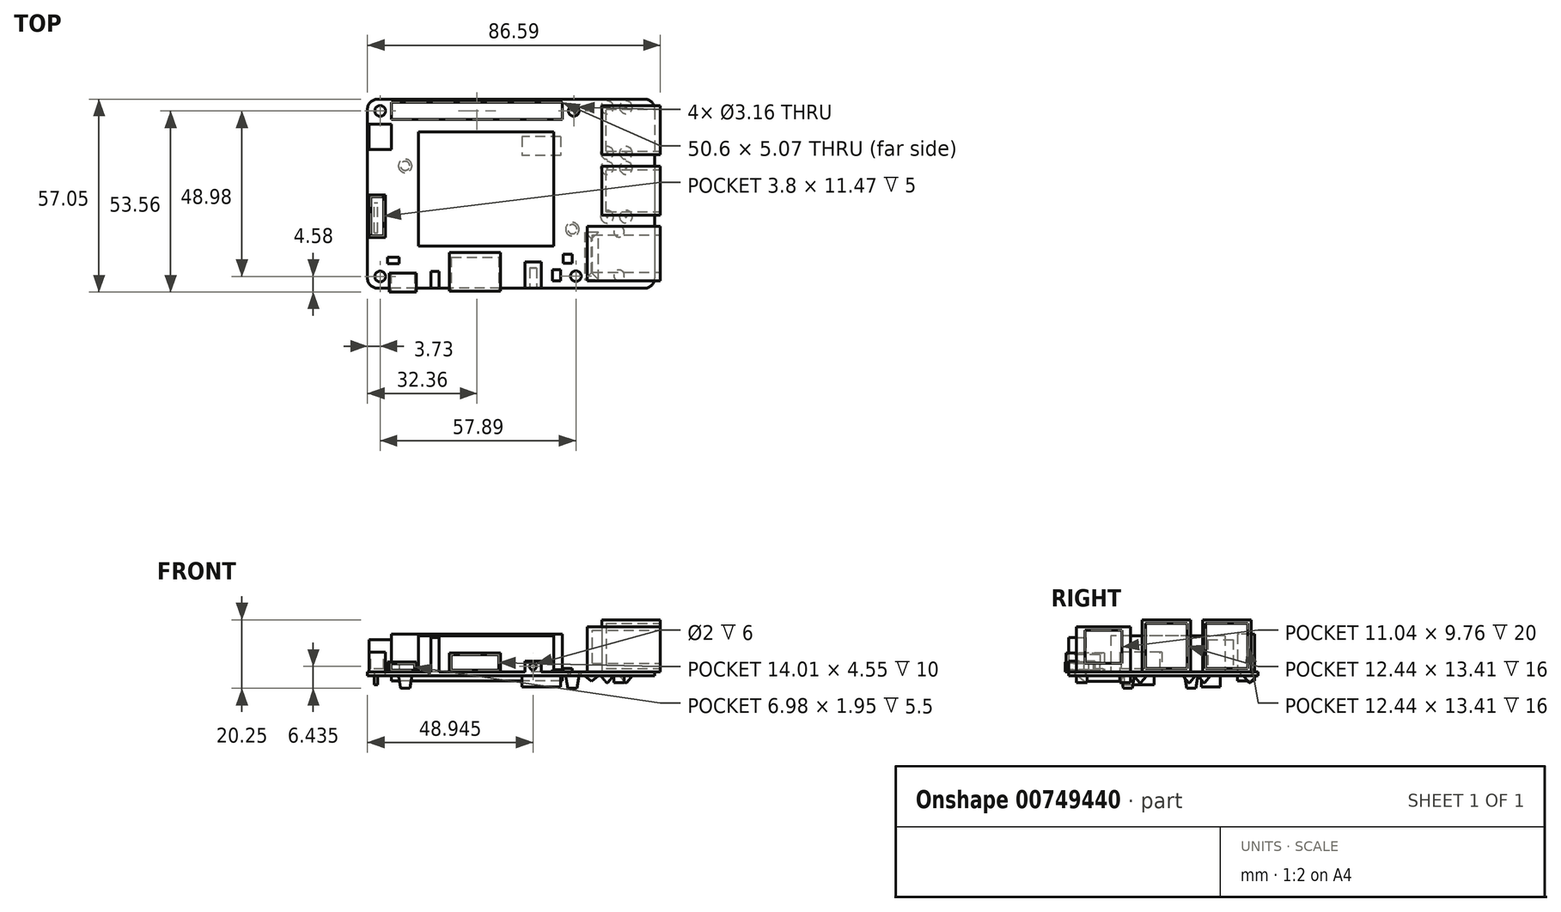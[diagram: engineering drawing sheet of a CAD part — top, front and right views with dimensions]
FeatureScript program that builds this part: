
annotation { "Feature Type Name" : "Feature", "Feature Type Description" : "" }
export const myFeature = defineFeature(function(context is Context, id is Id, definition is map)
    precondition{}
    {
        {
            var Q0;
            Q0=qCreatedBy(makeId("Top.planeOp"),FACE);
            var sketch = newSketch(context, id + "F0", { "sketchPlane" : qUnion([Q0])});
            skLineSegment(sketch, "E0.bottom", {"start": v(42.46, 27.98) * mm, "end": v(-42.46, 27.98) * mm});
            skLineSegment(sketch, "E0.top", {"start": v(42.46, -27.98) * mm, "end": v(-42.46, -27.98) * mm});
            skLineSegment(sketch, "E0.left", {"start": v(42.46, 27.98) * mm, "end": v(42.46, -27.98) * mm});
            skLineSegment(sketch, "E0.right", {"start": v(-42.46, 27.98) * mm, "end": v(-42.46, -27.98) * mm});
            skPoint(sketch, "E0.middle", {"position": v(0, 0) * mm});
            skSolve(sketch);
        }
        {
            var Q0;
            Q0 = qSketchRegion(id + "F0", true);
            extrude(context, id + "F1", {"entities" : qUnion([Q0]), "depth" : 1.15 * mm, "offsetDistance" : 25 * mm});
        }
        {
            var Q0;
            Q0=makeQuery(id+"F1.opExtrude","CAP_FACE",FACE,{"disambiguationData":[OSD([sQuery(id+"F0.wireOp",EDGE,"E0.bottom"),sQuery(id+"F0.wireOp",EDGE,"E0.top"),sQuery(id+"F0.wireOp",EDGE,"E0.left"),sQuery(id+"F0.wireOp",EDGE,"E0.right")])],"isStart":false});
            var sketch = newSketch(context, id + "F2", { "sketchPlane" : qUnion([Q0])});
            skLineSegment(sketch, "E1.top", {"start": v(44.05, -9.69) * mm, "end": v(22.48, -9.69) * mm});
            skLineSegment(sketch, "E1.left", {"start": v(44.05, -25.73) * mm, "end": v(44.05, -9.69) * mm});
            skLineSegment(sketch, "E1.right", {"start": v(22.48, -25.73) * mm, "end": v(22.48, -9.69) * mm});
            skLineSegment(sketch, "E2", {"start": v(44.05, -25.73) * mm, "end": v(22.48, -25.73) * mm});
            skSolve(sketch);
        }
        {
            var Q0;
            Q0 = qSketchRegion(id + "F2", true);
            extrude(context, id + "F3", {"entities" : qUnion([Q0]), "operationType" : NewBodyOperationType.ADD, "depth" : 13.33 * mm, "offsetDistance" : 25 * mm});
        }
        {
            var Q0;
            Q0=makeQuery(id+"F3.opExtrude","SWEPT_FACE",FACE,{"disambiguationData":[OSD([sQuery(id+"F2.wireOp",EDGE,"E1.left")])]});
            var sketch = newSketch(context, id + "F4", { "sketchPlane" : qUnion([Q0])});
            skLineSegment(sketch, "E3", {"start": v(-23.23, 13.45) * mm, "end": v(-12.19, 13.45) * mm});
            skLineSegment(sketch, "E4", {"start": v(-23.23, 3.7) * mm, "end": v(-23.23, 13.45) * mm});
            skLineSegment(sketch, "E5", {"start": v(-23.23, 3.7) * mm, "end": v(-12.19, 3.7) * mm});
            skLineSegment(sketch, "E6", {"start": v(-12.19, 3.7) * mm, "end": v(-12.19, 13.45) * mm});
            skSolve(sketch);
        }
        {
            var Q0;
            Q0 = qSketchRegion(id + "F4", true);
            extrude(context, id + "F5", {"entities" : qUnion([Q0]), "operationType" : NewBodyOperationType.REMOVE, "oppositeDirection" : true, "depth" : 20 * mm, "offsetDistance" : 25 * mm});
        }
        {
            var Q0;
            Q0=makeQuery(id+"F1.opExtrude","CAP_FACE",FACE,{"disambiguationData":[OSD([sQuery(id+"F0.wireOp",EDGE,"E0.bottom"),sQuery(id+"F0.wireOp",EDGE,"E0.top"),sQuery(id+"F0.wireOp",EDGE,"E0.left"),sQuery(id+"F0.wireOp",EDGE,"E0.right")])],"isStart":false});
            var sketch = newSketch(context, id + "F6", { "sketchPlane" : qUnion([Q0])});
            skLineSegment(sketch, "E7", {"start": v(42.46, -25.73) * mm, "end": v(42.46, 8.12) * mm});
            skLineSegment(sketch, "E8", {"start": v(42.46, 8.12) * mm, "end": v(44.13, 8.12) * mm});
            skLineSegment(sketch, "E9.bottom", {"start": v(44.13, 8.12) * mm, "end": v(26.87, 8.12) * mm});
            skLineSegment(sketch, "E9.top", {"start": v(44.13, -6.32) * mm, "end": v(26.87, -6.32) * mm});
            skLineSegment(sketch, "E9.left", {"start": v(44.13, 8.12) * mm, "end": v(44.13, -6.32) * mm});
            skLineSegment(sketch, "E9.right", {"start": v(26.87, 8.12) * mm, "end": v(26.87, -6.32) * mm});
            skLineSegment(sketch, "E10", {"start": v(42.46, -25.73) * mm, "end": v(42.46, 26.01) * mm});
            skLineSegment(sketch, "E11", {"start": v(42.46, 26.01) * mm, "end": v(44.13, 26.01) * mm});
            skLineSegment(sketch, "E12.bottom", {"start": v(44.13, 26.01) * mm, "end": v(26.87, 26.01) * mm});
            skLineSegment(sketch, "E12.top", {"start": v(44.13, 11.57) * mm, "end": v(26.87, 11.57) * mm});
            skLineSegment(sketch, "E12.left", {"start": v(44.13, 26.01) * mm, "end": v(44.13, 11.57) * mm});
            skLineSegment(sketch, "E12.right", {"start": v(26.87, 26.01) * mm, "end": v(26.87, 11.57) * mm});
            skSolve(sketch);
        }
        {
            var Q0;
            Q0 = qSketchRegion(id + "F6", true);
            extrude(context, id + "F7", {"entities" : qUnion([Q0]), "operationType" : NewBodyOperationType.ADD, "depth" : 15.4 * mm, "offsetDistance" : 25 * mm});
        }
        {
            var Q0;
            Q0=makeQuery(id+"F7.opExtrude","SWEPT_FACE",FACE,{"disambiguationData":[OSD([sQuery(id+"F6.wireOp",EDGE,"E9.left")])]});
            var sketch = newSketch(context, id + "F8", { "sketchPlane" : qUnion([Q0])});
            skLineSegment(sketch, "E13.bottom", {"start": v(-5.32, 15.56) * mm, "end": v(7.12, 15.56) * mm});
            skLineSegment(sketch, "E13.top", {"start": v(-5.32, 2.15) * mm, "end": v(7.12, 2.15) * mm});
            skLineSegment(sketch, "E13.left", {"start": v(-5.32, 15.56) * mm, "end": v(-5.32, 2.15) * mm});
            skLineSegment(sketch, "E13.right", {"start": v(7.12, 15.56) * mm, "end": v(7.12, 2.15) * mm});
            skSolve(sketch);
        }
        {
            var Q0;
            Q0 = qSketchRegion(id + "F8", true);
            extrude(context, id + "F9", {"entities" : qUnion([Q0]), "operationType" : NewBodyOperationType.REMOVE, "oppositeDirection" : true, "depth" : 16 * mm, "offsetDistance" : 25 * mm});
        }
        {
            var Q0;
            Q0=makeQuery(id+"F7.opExtrude","SWEPT_FACE",FACE,{"disambiguationData":[OSD([sQuery(id+"F6.wireOp",EDGE,"E12.left")])]});
            var sketch = newSketch(context, id + "F10", { "sketchPlane" : qUnion([Q0])});
            skLineSegment(sketch, "E14.bottom", {"start": v(12.57, 15.56) * mm, "end": v(25.01, 15.56) * mm});
            skLineSegment(sketch, "E14.top", {"start": v(12.57, 2.15) * mm, "end": v(25.01, 2.15) * mm});
            skLineSegment(sketch, "E14.left", {"start": v(12.57, 15.56) * mm, "end": v(12.57, 2.15) * mm});
            skLineSegment(sketch, "E14.right", {"start": v(25.01, 15.56) * mm, "end": v(25.01, 2.15) * mm});
            skSolve(sketch);
        }
        {
            var Q0;
            Q0 = qSketchRegion(id + "F10", true);
            extrude(context, id + "F11", {"entities" : qUnion([Q0]), "operationType" : NewBodyOperationType.REMOVE, "oppositeDirection" : true, "depth" : 16 * mm, "offsetDistance" : 25 * mm});
        }
        {
            var Q0;
            Q0=makeQuery(id+"F1.opExtrude","CAP_FACE",FACE,{"disambiguationData":[OSD([sQuery(id+"F0.wireOp",EDGE,"E0.bottom"),sQuery(id+"F0.wireOp",EDGE,"E0.top"),sQuery(id+"F0.wireOp",EDGE,"E0.left"),sQuery(id+"F0.wireOp",EDGE,"E0.right")])],"isStart":false});
            var sketch = newSketch(context, id + "F12", { "sketchPlane" : qUnion([Q0])});
            skLineSegment(sketch, "E15.bottom", {"start": v(15.2, 27.03) * mm, "end": v(-35.4, 27.03) * mm});
            skLineSegment(sketch, "E15.top", {"start": v(15.2, 21.96) * mm, "end": v(-35.4, 21.95) * mm});
            skLineSegment(sketch, "E15.left", {"start": v(15.2, 27.03) * mm, "end": v(15.2, 21.96) * mm});
            skLineSegment(sketch, "E15.right", {"start": v(-35.4, 27.02) * mm, "end": v(-35.4, 21.95) * mm});
            skSolve(sketch);
        }
        {
            var Q0;
            Q0 = qSketchRegion(id + "F12", true);
            extrude(context, id + "F13", {"entities" : qUnion([Q0]), "operationType" : NewBodyOperationType.ADD, "depth" : 11.21 * mm, "offsetDistance" : 25 * mm, "hasSecondDirection" : true, "secondDirectionOppositeDirection" : true, "secondDirectionDepth" : 2.67 * mm});
        }
        {
            var Q0;
            Q0=makeQuery(id+"F1.opExtrude","CAP_FACE",FACE,{"disambiguationData":[OSD([sQuery(id+"F0.wireOp",EDGE,"E0.bottom"),sQuery(id+"F0.wireOp",EDGE,"E0.top"),sQuery(id+"F0.wireOp",EDGE,"E0.left"),sQuery(id+"F0.wireOp",EDGE,"E0.right")])],"isStart":false});
            var sketch = newSketch(context, id + "F14", { "sketchPlane" : qUnion([Q0])});
            skLineSegment(sketch, "E16", {"start": v(-35.4, 24.5) * mm, "end": v(-37.15, 24.5) * mm});
            skLineSegment(sketch, "E17", {"start": v(-37.15, 24.5) * mm, "end": v(-38.73, 24.5) * mm});
            skLineSegment(sketch, "E18", {"start": v(15.2, 24.5) * mm, "end": v(16.95, 24.5) * mm});
            skLineSegment(sketch, "E19", {"start": v(16.95, 24.5) * mm, "end": v(18.53, 24.5) * mm});
            skCircle(sketch, "E20", {"center": v(18.53, 24.5) * mm, "radius": 1.58 * mm});
            skLineSegment(sketch, "E21", {"start": v(-42.46, 0) * mm, "end": v(60.27, 0) * mm});
            skLineSegment(sketch, "E22", {"start": v(22.48, -25.73) * mm, "end": v(20.74, -25.73) * mm});
            skLineSegment(sketch, "E23", {"start": v(20.74, -25.73) * mm, "end": v(20.74, -18.8) * mm});
            skCircle(sketch, "E24", {"center": v(-38.73, 24.5) * mm, "radius": 1.58 * mm});
            skCircle(sketch, "E25.MirrorC", {"center": v(-38.73, -24.5) * mm, "radius": 1.58 * mm});
            skLineSegment(sketch, "E26", {"start": v(19.4, -27.98) * mm, "end": v(19.4, -25.98) * mm});
            skLineSegment(sketch, "E27", {"start": v(19.4, -24.4) * mm, "end": v(16.42, -24.4) * mm});
            skCircle(sketch, "E28", {"center": v(19.16, -24.4) * mm, "radius": 1.58 * mm});
            skSolve(sketch);
        }
        {
            var Q0;
            Q0 = qSketchRegion(id + "F14", true);
            extrude(context, id + "F15", {"entities" : qUnion([Q0]), "operationType" : NewBodyOperationType.REMOVE, "endBound" : BoundingType.THROUGH_ALL, "oppositeDirection" : true, "depth" : 25 * mm, "offsetDistance" : 25 * mm});
        }
        {
            var Q0;
            Q0=makeQuery(id+"F1.opExtrude","CAP_FACE",FACE,{"disambiguationData":[OSD([sQuery(id+"F0.wireOp",EDGE,"E0.bottom"),sQuery(id+"F0.wireOp",EDGE,"E0.top"),sQuery(id+"F0.wireOp",EDGE,"E0.left"),sQuery(id+"F0.wireOp",EDGE,"E0.right")])],"isStart":false});
            var sketch = newSketch(context, id + "F16", { "sketchPlane" : qUnion([Q0])});
            skLineSegment(sketch, "E29", {"start": v(-42.46, 27.98) * mm, "end": v(-42.46, 13.12) * mm});
            skLineSegment(sketch, "E30", {"start": v(-41.96, 13.12) * mm, "end": v(-35.4, 13.12) * mm});
            skLineSegment(sketch, "E31", {"start": v(-35.4, 20.59) * mm, "end": v(-35.4, 13.12) * mm});
            skLineSegment(sketch, "E32", {"start": v(-41.96, 13.12) * mm, "end": v(-41.96, 20.59) * mm});
            skLineSegment(sketch, "E33", {"start": v(-41.96, 20.59) * mm, "end": v(-35.4, 20.59) * mm});
            skSolve(sketch);
        }
        {
            var Q0;
            Q0 = qSketchRegion(id + "F16", true);
            extrude(context, id + "F17", {"entities" : qUnion([Q0]), "operationType" : NewBodyOperationType.ADD, "depth" : 9.58 * mm, "offsetDistance" : 25 * mm});
        }
        {
            var Q0;
            Q0=makeQuery(id+"F1.opExtrude","CAP_FACE",FACE,{"disambiguationData":[OSD([sQuery(id+"F0.wireOp",EDGE,"E0.bottom"),sQuery(id+"F0.wireOp",EDGE,"E0.top"),sQuery(id+"F0.wireOp",EDGE,"E0.left"),sQuery(id+"F0.wireOp",EDGE,"E0.right")])],"isStart":false});
            var sketch = newSketch(context, id + "F18", { "sketchPlane" : qUnion([Q0])});
            skLineSegment(sketch, "E34", {"start": v(-42.46, -27.98) * mm, "end": v(-42.46, -0.43) * mm});
            skLineSegment(sketch, "E35", {"start": v(-42.46, -0.43) * mm, "end": v(-41.96, -0.43) * mm});
            skLineSegment(sketch, "E36.bottom", {"start": v(-41.96, -0.43) * mm, "end": v(-37.16, -0.43) * mm});
            skLineSegment(sketch, "E36.top", {"start": v(-41.96, -12.9) * mm, "end": v(-37.16, -12.9) * mm});
            skLineSegment(sketch, "E36.left", {"start": v(-41.96, -0.43) * mm, "end": v(-41.96, -12.9) * mm});
            skLineSegment(sketch, "E36.right", {"start": v(-37.16, -0.43) * mm, "end": v(-37.16, -12.9) * mm});
            skSolve(sketch);
        }
        {
            var Q0;
            Q0 = qSketchRegion(id + "F18", true);
            extrude(context, id + "F19", {"entities" : qUnion([Q0]), "operationType" : NewBodyOperationType.ADD, "depth" : 5.87 * mm, "offsetDistance" : 25 * mm});
        }
        {
            var Q0;
            Q0=makeQuery(id+"F19.opExtrude","CAP_FACE",FACE,{"disambiguationData":[OSD([sQuery(id+"F18.wireOp",EDGE,"E36.bottom"),sQuery(id+"F18.wireOp",EDGE,"E36.top"),sQuery(id+"F18.wireOp",EDGE,"E36.left"),sQuery(id+"F18.wireOp",EDGE,"E36.right")])],"isStart":false});
            var sketch = newSketch(context, id + "F20", { "sketchPlane" : qUnion([Q0])});
            skLineSegment(sketch, "E37.bottom", {"start": v(-37.16, -0.43) * mm, "end": v(-37.66, -0.43) * mm});
            skLineSegment(sketch, "E37.left", {"start": v(-37.16, -0.43) * mm, "end": v(-37.16, -0.93) * mm});
            skLineSegment(sketch, "E37.right", {"start": v(-37.66, -0.43) * mm, "end": v(-37.66, -0.93) * mm});
            skLineSegment(sketch, "E38.bottom", {"start": v(-41.96, -12.9) * mm, "end": v(-41.46, -12.9) * mm});
            skLineSegment(sketch, "E38.left", {"start": v(-41.96, -12.9) * mm, "end": v(-41.96, -12.4) * mm});
            skLineSegment(sketch, "E38.right", {"start": v(-41.46, -12.9) * mm, "end": v(-41.46, -12.4) * mm});
            skLineSegment(sketch, "E39.bottom", {"start": v(-37.66, -0.93) * mm, "end": v(-41.46, -0.93) * mm});
            skLineSegment(sketch, "E39.top", {"start": v(-37.66, -12.4) * mm, "end": v(-41.46, -12.4) * mm});
            skLineSegment(sketch, "E39.left", {"start": v(-37.66, -0.93) * mm, "end": v(-37.66, -12.4) * mm});
            skLineSegment(sketch, "E39.right", {"start": v(-41.46, -0.93) * mm, "end": v(-41.46, -12.4) * mm});
            skSolve(sketch);
        }
        {
            var Q0;
            Q0 = qSketchRegion(id + "F20", true);
            extrude(context, id + "F21", {"entities" : qUnion([Q0]), "operationType" : NewBodyOperationType.REMOVE, "oppositeDirection" : true, "depth" : 5 * mm, "offsetDistance" : 25 * mm});
        }
        {
            var Q0;
            Q0=makeQuery(id+"F1.opExtrude","CAP_FACE",FACE,{"disambiguationData":[OSD([sQuery(id+"F0.wireOp",EDGE,"E0.bottom"),sQuery(id+"F0.wireOp",EDGE,"E0.top"),sQuery(id+"F0.wireOp",EDGE,"E0.left"),sQuery(id+"F0.wireOp",EDGE,"E0.right")])],"isStart":false});
            var sketch = newSketch(context, id + "F22", { "sketchPlane" : qUnion([Q0])});
            skLineSegment(sketch, "E40.0", {"start": v(44.05, -25.73) * mm, "end": v(44.05, -9.69) * mm});
            skLineSegment(sketch, "E41", {"start": v(44.05, -25.73) * mm, "end": v(8.9, -25.73) * mm});
            skLineSegment(sketch, "E42.bottom", {"start": v(4.06, -27.98) * mm, "end": v(8.9, -27.98) * mm});
            skLineSegment(sketch, "E42.top", {"start": v(4.06, -20.23) * mm, "end": v(8.9, -20.23) * mm});
            skLineSegment(sketch, "E43", {"start": v(4.06, -20.23) * mm, "end": v(4.06, -27.98) * mm});
            skLineSegment(sketch, "E44", {"start": v(8.9, -20.23) * mm, "end": v(8.9, -27.98) * mm});
            skSolve(sketch);
        }
        {
            var Q0;
            Q0 = qSketchRegion(id + "F22", true);
            extrude(context, id + "F23", {"entities" : qUnion([Q0]), "operationType" : NewBodyOperationType.ADD, "depth" : 3.19 * mm, "offsetDistance" : 25 * mm});
        }
        {
            var Q0;
            Q0=makeQuery(id+"F23.boolean.opBoolean","MERGE",FACE,{"derivedFrom":[makeQuery(id+"F1.opExtrude","SWEPT_FACE",FACE,{"disambiguationData":[OSD([sQuery(id+"F0.wireOp",EDGE,"E0.top")])]}),makeQuery(id+"F23.opExtrude","SWEPT_FACE",FACE,{"disambiguationData":[OSD([sQuery(id+"F22.wireOp",EDGE,"E42.bottom")])]})]});
            var sketch = newSketch(context, id + "F24", { "sketchPlane" : qUnion([Q0])});
            skCircle(sketch, "E45", {"center": v(6.48, 2.75) * mm, "radius": 1 * mm});
            skSolve(sketch);
        }
        {
            var Q0;
            Q0 = qSketchRegion(id + "F24", true);
            extrude(context, id + "F25", {"entities" : qUnion([Q0]), "operationType" : NewBodyOperationType.REMOVE, "oppositeDirection" : true, "depth" : 6 * mm, "offsetDistance" : 25 * mm});
        }
        {
            var Q0;
            Q0=makeQuery(id+"F1.opExtrude","CAP_FACE",FACE,{"disambiguationData":[OSD([sQuery(id+"F0.wireOp",EDGE,"E0.bottom"),sQuery(id+"F0.wireOp",EDGE,"E0.top"),sQuery(id+"F0.wireOp",EDGE,"E0.left"),sQuery(id+"F0.wireOp",EDGE,"E0.right")])],"isStart":false});
            var sketch = newSketch(context, id + "F26", { "sketchPlane" : qUnion([Q0])});
            skLineSegment(sketch, "E46.0", {"start": v(44.05, -25.73) * mm, "end": v(44.05, -9.69) * mm});
            skLineSegment(sketch, "E47", {"start": v(44.05, -25.73) * mm, "end": v(-21.29, -25.73) * mm});
            skLineSegment(sketch, "E48", {"start": v(-23.69, -25.73) * mm, "end": v(-23.69, -31.98) * mm});
            skLineSegment(sketch, "E49.bottom", {"start": v(-23.69, -27.98) * mm, "end": v(-21.29, -27.98) * mm});
            skLineSegment(sketch, "E49.top", {"start": v(-23.69, -22.95) * mm, "end": v(-21.29, -22.95) * mm});
            skLineSegment(sketch, "E49.left", {"start": v(-23.69, -27.98) * mm, "end": v(-23.69, -22.95) * mm});
            skLineSegment(sketch, "E49.right", {"start": v(-21.29, -27.98) * mm, "end": v(-21.29, -22.95) * mm});
            skSolve(sketch);
        }
        {
            var Q0;
            Q0 = qSketchRegion(id + "F26", true);
            extrude(context, id + "F27", {"entities" : qUnion([Q0]), "operationType" : NewBodyOperationType.ADD, "depth" : 10.1 * mm, "offsetDistance" : 25 * mm});
        }
        {
            var Q0;
            Q0=makeQuery(id+"F1.opExtrude","CAP_FACE",FACE,{"disambiguationData":[OSD([sQuery(id+"F0.wireOp",EDGE,"E0.bottom"),sQuery(id+"F0.wireOp",EDGE,"E0.top"),sQuery(id+"F0.wireOp",EDGE,"E0.left"),sQuery(id+"F0.wireOp",EDGE,"E0.right")])],"isStart":false});
            var sketch = newSketch(context, id + "F28", { "sketchPlane" : qUnion([Q0])});
            skLineSegment(sketch, "E50", {"start": v(-21.29, -27.98) * mm, "end": v(-18.19, -27.98) * mm});
            skLineSegment(sketch, "E51", {"start": v(-18.19, -27.98) * mm, "end": v(-18.19, -28.78) * mm});
            skLineSegment(sketch, "E52.bottom", {"start": v(-18.19, -28.78) * mm, "end": v(-3.18, -28.78) * mm});
            skLineSegment(sketch, "E52.top", {"start": v(-18.19, -17.4) * mm, "end": v(-3.18, -17.4) * mm});
            skLineSegment(sketch, "E52.left", {"start": v(-18.19, -28.78) * mm, "end": v(-18.19, -17.4) * mm});
            skLineSegment(sketch, "E52.right", {"start": v(-3.18, -28.78) * mm, "end": v(-3.18, -17.4) * mm});
            skSolve(sketch);
        }
        {
            var Q0;
            Q0 = qSketchRegion(id + "F28", true);
            extrude(context, id + "F29", {"entities" : qUnion([Q0]), "operationType" : NewBodyOperationType.ADD, "depth" : 5.55 * mm, "offsetDistance" : 25 * mm});
        }
        {
            var Q0;
            Q0=makeQuery(id+"F29.opExtrude","SWEPT_FACE",FACE,{"disambiguationData":[OSD([sQuery(id+"F28.wireOp",EDGE,"E52.bottom")])]});
            var sketch = newSketch(context, id + "F30", { "sketchPlane" : qUnion([Q0])});
            skLineSegment(sketch, "E53.bottom", {"start": v(-18.19, 6.7) * mm, "end": v(-17.69, 6.7) * mm});
            skLineSegment(sketch, "E53.left", {"start": v(-18.19, 6.7) * mm, "end": v(-18.19, 6.2) * mm});
            skLineSegment(sketch, "E53.right", {"start": v(-17.69, 6.7) * mm, "end": v(-17.69, 6.2) * mm});
            skLineSegment(sketch, "E54.bottom", {"start": v(-3.18, 1.15) * mm, "end": v(-3.68, 1.15) * mm});
            skLineSegment(sketch, "E54.left", {"start": v(-3.18, 1.15) * mm, "end": v(-3.18, 1.65) * mm});
            skLineSegment(sketch, "E54.right", {"start": v(-3.68, 1.15) * mm, "end": v(-3.68, 1.65) * mm});
            skLineSegment(sketch, "E55.bottom", {"start": v(-17.69, 6.2) * mm, "end": v(-3.68, 6.2) * mm});
            skLineSegment(sketch, "E55.top", {"start": v(-17.69, 1.65) * mm, "end": v(-3.68, 1.65) * mm});
            skLineSegment(sketch, "E55.left", {"start": v(-17.69, 6.2) * mm, "end": v(-17.69, 1.65) * mm});
            skLineSegment(sketch, "E55.right", {"start": v(-3.68, 6.2) * mm, "end": v(-3.68, 1.65) * mm});
            skSolve(sketch);
        }
        {
            var Q0;
            Q0 = qSketchRegion(id + "F30", true);
            extrude(context, id + "F31", {"entities" : qUnion([Q0]), "operationType" : NewBodyOperationType.REMOVE, "oppositeDirection" : true, "depth" : 10 * mm, "offsetDistance" : 25 * mm});
        }
        {
            var Q0;
            Q0=makeQuery(id+"F1.opExtrude","CAP_FACE",FACE,{"disambiguationData":[OSD([sQuery(id+"F0.wireOp",EDGE,"E0.bottom"),sQuery(id+"F0.wireOp",EDGE,"E0.top"),sQuery(id+"F0.wireOp",EDGE,"E0.left"),sQuery(id+"F0.wireOp",EDGE,"E0.right")])],"isStart":false});
            var sketch = newSketch(context, id + "F32", { "sketchPlane" : qUnion([Q0])});
            skLineSegment(sketch, "E56", {"start": v(-42.46, -27.98) * mm, "end": v(-35.98, -27.98) * mm});
            skLineSegment(sketch, "E57", {"start": v(-28, -27.98) * mm, "end": v(-28, -29.07) * mm});
            skLineSegment(sketch, "E58.bottom", {"start": v(-28, -29.07) * mm, "end": v(-35.98, -29.07) * mm});
            skLineSegment(sketch, "E58.top", {"start": v(-28, -23.52) * mm, "end": v(-35.98, -23.52) * mm});
            skLineSegment(sketch, "E58.left", {"start": v(-28, -29.07) * mm, "end": v(-28, -23.52) * mm});
            skLineSegment(sketch, "E58.right", {"start": v(-35.98, -29.08) * mm, "end": v(-35.98, -23.52) * mm});
            skSolve(sketch);
        }
        {
            var Q0;
            Q0 = qSketchRegion(id + "F32", true);
            extrude(context, id + "F33", {"entities" : qUnion([Q0]), "operationType" : NewBodyOperationType.ADD, "depth" : 2.95 * mm, "offsetDistance" : 25 * mm});
        }
        {
            var Q0;
            Q0=makeQuery(id+"F1.opExtrude","CAP_FACE",FACE,{"disambiguationData":[OSD([sQuery(id+"F0.wireOp",EDGE,"E0.bottom"),sQuery(id+"F0.wireOp",EDGE,"E0.top"),sQuery(id+"F0.wireOp",EDGE,"E0.left"),sQuery(id+"F0.wireOp",EDGE,"E0.right")])],"isStart":false});
            var sketch = newSketch(context, id + "F34", { "sketchPlane" : qUnion([Q0])});
            skLineSegment(sketch, "E59", {"start": v(-35.98, -23.52) * mm, "end": v(-35.98, -20.7) * mm});
            skLineSegment(sketch, "E60", {"start": v(-35.98, -20.7) * mm, "end": v(-36.48, -20.7) * mm});
            skLineSegment(sketch, "E61.bottom", {"start": v(-36.48, -20.7) * mm, "end": v(-33.11, -20.7) * mm});
            skLineSegment(sketch, "E61.top", {"start": v(-36.48, -18.8) * mm, "end": v(-33.11, -18.8) * mm});
            skLineSegment(sketch, "E61.left", {"start": v(-36.48, -20.7) * mm, "end": v(-36.48, -18.8) * mm});
            skLineSegment(sketch, "E61.right", {"start": v(-33.11, -20.7) * mm, "end": v(-33.11, -18.8) * mm});
            skSolve(sketch);
        }
        {
            var Q0;
            Q0 = qSketchRegion(id + "F34", true);
            extrude(context, id + "F35", {"entities" : qUnion([Q0]), "operationType" : NewBodyOperationType.ADD, "depth" : 2.96 * mm, "offsetDistance" : 25 * mm});
        }
        {
            var Q0;
            Q0=makeQuery(id+"F33.opExtrude","SWEPT_FACE",FACE,{"disambiguationData":[OSD([sQuery(id+"F32.wireOp",EDGE,"E58.bottom")])]});
            var sketch = newSketch(context, id + "F36", { "sketchPlane" : qUnion([Q0])});
            skLineSegment(sketch, "E62.bottom", {"start": v(-35.48, 3.6) * mm, "end": v(-28.5, 3.6) * mm});
            skLineSegment(sketch, "E62.top", {"start": v(-35.48, 1.65) * mm, "end": v(-28.5, 1.65) * mm});
            skLineSegment(sketch, "E62.left", {"start": v(-35.48, 3.6) * mm, "end": v(-35.48, 1.65) * mm});
            skLineSegment(sketch, "E62.right", {"start": v(-28.5, 3.6) * mm, "end": v(-28.5, 1.65) * mm});
            skSolve(sketch);
        }
        {
            var Q0;
            Q0 = qSketchRegion(id + "F36", true);
            extrude(context, id + "F37", {"entities" : qUnion([Q0]), "operationType" : NewBodyOperationType.REMOVE, "oppositeDirection" : true, "depth" : 5.5 * mm, "offsetDistance" : 25 * mm});
        }
        {
            var Q0;
            Q0=makeQuery(id+"F1.opExtrude","CAP_FACE",FACE,{"disambiguationData":[OSD([sQuery(id+"F0.wireOp",EDGE,"E0.bottom"),sQuery(id+"F0.wireOp",EDGE,"E0.top"),sQuery(id+"F0.wireOp",EDGE,"E0.left"),sQuery(id+"F0.wireOp",EDGE,"E0.right")])],"isStart":false});
            var sketch = newSketch(context, id + "F38", { "sketchPlane" : qUnion([Q0])});
            skLineSegment(sketch, "E63", {"start": v(19.4, -25.73) * mm, "end": v(18.06, -25.73) * mm});
            skLineSegment(sketch, "E64", {"start": v(18.06, -25.73) * mm, "end": v(14.65, -25.73) * mm});
            skLineSegment(sketch, "E65.bottom", {"start": v(14.65, -25.73) * mm, "end": v(12.19, -25.73) * mm});
            skLineSegment(sketch, "E65.top", {"start": v(14.65, -22.53) * mm, "end": v(12.19, -22.53) * mm});
            skLineSegment(sketch, "E65.left", {"start": v(14.65, -25.73) * mm, "end": v(14.65, -22.53) * mm});
            skLineSegment(sketch, "E65.right", {"start": v(12.19, -25.73) * mm, "end": v(12.19, -22.53) * mm});
            skSolve(sketch);
        }
        {
            var Q0;
            Q0 = qSketchRegion(id + "F38", true);
            extrude(context, id + "F39", {"entities" : qUnion([Q0]), "operationType" : NewBodyOperationType.ADD, "depth" : 0.6 * mm, "offsetDistance" : 25 * mm});
        }
        {
            var Q0;
            Q0=makeQuery(id+"F1.opExtrude","CAP_FACE",FACE,{"disambiguationData":[OSD([sQuery(id+"F0.wireOp",EDGE,"E0.bottom"),sQuery(id+"F0.wireOp",EDGE,"E0.top"),sQuery(id+"F0.wireOp",EDGE,"E0.left"),sQuery(id+"F0.wireOp",EDGE,"E0.right")])],"isStart":false});
            var sketch = newSketch(context, id + "F40", { "sketchPlane" : qUnion([Q0])});
            skLineSegment(sketch, "E66", {"start": v(14.65, -22.53) * mm, "end": v(14.65, -20.53) * mm});
            skLineSegment(sketch, "E67", {"start": v(19.4, -25.73) * mm, "end": v(18.06, -25.73) * mm});
            skLineSegment(sketch, "E68.bottom", {"start": v(18.06, -20.53) * mm, "end": v(15.43, -20.53) * mm});
            skLineSegment(sketch, "E68.top", {"start": v(18.06, -17.9) * mm, "end": v(15.43, -17.9) * mm});
            skLineSegment(sketch, "E68.left", {"start": v(18.06, -20.53) * mm, "end": v(18.06, -17.9) * mm});
            skLineSegment(sketch, "E68.right", {"start": v(15.43, -20.53) * mm, "end": v(15.43, -17.9) * mm});
            skSolve(sketch);
        }
        {
            var Q0;
            Q0 = qSketchRegion(id + "F40", true);
            extrude(context, id + "F41", {"entities" : qUnion([Q0]), "operationType" : NewBodyOperationType.ADD, "depth" : 1 * mm, "offsetDistance" : 25 * mm});
        }
        {
            var Q0;
            Q0=makeQuery(id+"F1.opExtrude","CAP_FACE",FACE,{"disambiguationData":[OSD([sQuery(id+"F0.wireOp",EDGE,"E0.bottom"),sQuery(id+"F0.wireOp",EDGE,"E0.top"),sQuery(id+"F0.wireOp",EDGE,"E0.left"),sQuery(id+"F0.wireOp",EDGE,"E0.right")])],"isStart":false});
            var sketch = newSketch(context, id + "F42", { "sketchPlane" : qUnion([Q0])});
            skLineSegment(sketch, "E69", {"start": v(15.2, 21.96) * mm, "end": v(15.2, 18.27) * mm});
            skLineSegment(sketch, "E70.0", {"start": v(-35.4, 27.03) * mm, "end": v(-35.4, 21.95) * mm});
            skLineSegment(sketch, "E71.0", {"start": v(15.2, 27.03) * mm, "end": v(15.2, 21.96) * mm});
            skLineSegment(sketch, "E72", {"start": v(15.2, 18.27) * mm, "end": v(12.67, 18.27) * mm});
            skLineSegment(sketch, "E73.bottom", {"start": v(12.67, 18.27) * mm, "end": v(-27.34, 18.27) * mm});
            skLineSegment(sketch, "E73.top", {"start": v(12.67, -15.54) * mm, "end": v(-27.34, -15.54) * mm});
            skLineSegment(sketch, "E73.left", {"start": v(12.67, 18.27) * mm, "end": v(12.67, -15.54) * mm});
            skLineSegment(sketch, "E73.right", {"start": v(-27.34, 18.27) * mm, "end": v(-27.34, -15.54) * mm});
            skSolve(sketch);
        }
        {
            var Q0;
            Q0 = qSketchRegion(id + "F42", true);
            extrude(context, id + "F43", {"entities" : qUnion([Q0]), "operationType" : NewBodyOperationType.ADD, "depth" : 10.71 * mm, "offsetDistance" : 25 * mm});
        }
        {
            var Q0;
            Q0=makeQuery(id+"F1.opExtrude","CAP_FACE",FACE,{"disambiguationData":[OSD([sQuery(id+"F0.wireOp",EDGE,"E0.bottom"),sQuery(id+"F0.wireOp",EDGE,"E0.top"),sQuery(id+"F0.wireOp",EDGE,"E0.left"),sQuery(id+"F0.wireOp",EDGE,"E0.right")])],"isStart":true});
            var sketch = newSketch(context, id + "F44", { "sketchPlane" : qUnion([Q0])});
            skLineSegment(sketch, "E74.bottom", {"start": v(-40.46, 11.5) * mm, "end": v(-39.46, 11.5) * mm});
            skLineSegment(sketch, "E74.top", {"start": v(-40.46, 2.73) * mm, "end": v(-39.46, 2.73) * mm});
            skLineSegment(sketch, "E74.right", {"start": v(-39.46, 11.5) * mm, "end": v(-39.46, 2.73) * mm});
            skLineSegment(sketch, "E75", {"start": v(-40.46, 11.5) * mm, "end": v(-40.46, 2.73) * mm});
            skSolve(sketch);
        }
        {
            var Q0;
            Q0 = qSketchRegion(id + "F44", true);
            extrude(context, id + "F45", {"entities" : qUnion([Q0]), "operationType" : NewBodyOperationType.ADD, "depth" : 2.67 * mm, "offsetDistance" : 25 * mm});
        }
        {
            var Q0;
            Q0=makeQuery(id+"F1.opExtrude","CAP_FACE",FACE,{"disambiguationData":[OSD([sQuery(id+"F0.wireOp",EDGE,"E0.bottom"),sQuery(id+"F0.wireOp",EDGE,"E0.top"),sQuery(id+"F0.wireOp",EDGE,"E0.left"),sQuery(id+"F0.wireOp",EDGE,"E0.right")])],"isStart":true});
            var sketch = newSketch(context, id + "F46", { "sketchPlane" : qUnion([Q0])});
            skCircle(sketch, "E76", {"center": v(33.97, -25.56) * mm, "radius": 1.89 * mm});
            skCircle(sketch, "E77.MirrorC", {"center": v(28.4, -25.56) * mm, "radius": 1.89 * mm});
            skPoint(sketch, "E78.0.end.orphan", {"position": v(42.46, -11.57) * mm});
            skPoint(sketch, "E78.0.start.orphan", {"position": v(44.13, -11.57) * mm});
            skLineSegment(sketch, "E79.0", {"start": v(44.13, -8.12) * mm, "end": v(42.46, -8.12) * mm});
            skLineSegment(sketch, "E80.0", {"start": v(44.13, 6.32) * mm, "end": v(42.46, 6.32) * mm});
            skLineSegment(sketch, "E81.0", {"start": v(44.13, -11.57) * mm, "end": v(42.46, -11.57) * mm});
            skCircle(sketch, "E82", {"center": v(33.97, -12.07) * mm, "radius": 1.89 * mm});
            skCircle(sketch, "E83", {"center": v(28.4, -12.07) * mm, "radius": 1.89 * mm});
            skCircle(sketch, "E84", {"center": v(33.97, -7.62) * mm, "radius": 1.89 * mm});
            skCircle(sketch, "E85", {"center": v(28.4, -7.62) * mm, "radius": 1.89 * mm});
            skCircle(sketch, "E86", {"center": v(33.97, 6.82) * mm, "radius": 1.89 * mm});
            skCircle(sketch, "E87", {"center": v(28.4, 6.82) * mm, "radius": 1.89 * mm});
            skSolve(sketch);
        }
        {
            var Q0;
            Q0 = qSketchRegion(id + "F46", true);
            extrude(context, id + "F47", {"entities" : qUnion([Q0]), "operationType" : NewBodyOperationType.ADD, "depth" : 2 * mm, "offsetDistance" : 25 * mm, "hasDraft" : true, "draftAngle" : 40 * degree, "draftPullDirection" : true});
        }
        {
            var Q0;
            Q0=makeQuery(id+"F1.opExtrude","CAP_FACE",FACE,{"disambiguationData":[OSD([sQuery(id+"F0.wireOp",EDGE,"E0.bottom"),sQuery(id+"F0.wireOp",EDGE,"E0.top"),sQuery(id+"F0.wireOp",EDGE,"E0.left"),sQuery(id+"F0.wireOp",EDGE,"E0.right")])],"isStart":true});
            var sketch = newSketch(context, id + "F48", { "sketchPlane" : qUnion([Q0])});
            skLineSegment(sketch, "E88.bottom", {"start": v(14.7, -16.86) * mm, "end": v(3.15, -16.86) * mm});
            skLineSegment(sketch, "E88.top", {"start": v(14.7, -11.3) * mm, "end": v(3.15, -11.3) * mm});
            skLineSegment(sketch, "E88.left", {"start": v(14.7, -16.86) * mm, "end": v(14.7, -11.3) * mm});
            skLineSegment(sketch, "E88.right", {"start": v(3.15, -16.86) * mm, "end": v(3.15, -11.3) * mm});
            skSolve(sketch);
        }
        {
            var Q0;
            Q0 = qSketchRegion(id + "F48", true);
            extrude(context, id + "F49", {"entities" : qUnion([Q0]), "operationType" : NewBodyOperationType.ADD, "depth" : 3.24 * mm, "offsetDistance" : 25 * mm});
        }
        {
            var Q0;
            Q0=makeQuery(id+"F1.opExtrude","CAP_FACE",FACE,{"disambiguationData":[OSD([sQuery(id+"F0.wireOp",EDGE,"E0.bottom"),sQuery(id+"F0.wireOp",EDGE,"E0.top"),sQuery(id+"F0.wireOp",EDGE,"E0.left"),sQuery(id+"F0.wireOp",EDGE,"E0.right")])],"isStart":true});
            var sketch = newSketch(context, id + "F50", { "sketchPlane" : qUnion([Q0])});
            skLineSegment(sketch, "E89", {"start": v(42.46, 25.73) * mm, "end": v(31.92, 25.73) * mm});
            skLineSegment(sketch, "E90", {"start": v(31.92, 25.73) * mm, "end": v(31.92, 24.16) * mm});
            skCircle(sketch, "E91", {"center": v(31.92, 24.16) * mm, "radius": 1.57 * mm});
            skLineSegment(sketch, "E92", {"start": v(31.92, 9.69) * mm, "end": v(31.92, 11.26) * mm});
            skCircle(sketch, "E93", {"center": v(31.92, 11.26) * mm, "radius": 1.57 * mm});
            skSolve(sketch);
        }
        {
            var Q0;
            Q0 = qSketchRegion(id + "F50", true);
            extrude(context, id + "F51", {"entities" : qUnion([Q0]), "operationType" : NewBodyOperationType.ADD, "depth" : 2.06 * mm, "offsetDistance" : 25 * mm});
        }
        {
            var Q0;
            Q0=makeQuery(id+"F1.opExtrude","CAP_FACE",FACE,{"disambiguationData":[OSD([sQuery(id+"F0.wireOp",EDGE,"E0.bottom"),sQuery(id+"F0.wireOp",EDGE,"E0.top"),sQuery(id+"F0.wireOp",EDGE,"E0.left"),sQuery(id+"F0.wireOp",EDGE,"E0.right")])],"isStart":true});
            var sketch = newSketch(context, id + "F52", { "sketchPlane" : qUnion([Q0])});
            skLineSegment(sketch, "E94", {"start": v(25.84, 11.38) * mm, "end": v(29.02, 11.38) * mm});
            skPoint(sketch, "E95", {"position": v(25.84, 11.38) * mm});
            skLineSegment(sketch, "E96.bottom", {"start": v(25.84, 11.38) * mm, "end": v(21.8, 11.38) * mm});
            skLineSegment(sketch, "E96.top", {"start": v(25.84, 25.41) * mm, "end": v(21.8, 25.41) * mm});
            skLineSegment(sketch, "E96.left", {"start": v(25.84, 11.38) * mm, "end": v(25.84, 25.41) * mm});
            skLineSegment(sketch, "E96.right", {"start": v(21.8, 11.38) * mm, "end": v(21.8, 25.41) * mm});
            skSolve(sketch);
        }
        {
            var Q0;
            Q0 = qSketchRegion(id + "F52", true);
            extrude(context, id + "F53", {"entities" : qUnion([Q0]), "operationType" : NewBodyOperationType.ADD, "depth" : 1.76 * mm, "offsetDistance" : 25 * mm, "hasDraft" : true, "draftAngle" : 50 * degree, "draftPullDirection" : true});
        }
        {
            var Q0;
            Q0=makeQuery(id+"F1.opExtrude","CAP_FACE",FACE,{"disambiguationData":[OSD([sQuery(id+"F0.wireOp",EDGE,"E0.bottom"),sQuery(id+"F0.wireOp",EDGE,"E0.top"),sQuery(id+"F0.wireOp",EDGE,"E0.left"),sQuery(id+"F0.wireOp",EDGE,"E0.right")])],"isStart":true});
            var sketch = newSketch(context, id + "F54", { "sketchPlane" : qUnion([Q0])});
            skLineSegment(sketch, "E97.bottom", {"start": v(-42.46, -27.98) * mm, "end": v(-31.32, -27.98) * mm});
            skLineSegment(sketch, "E97.left", {"start": v(-42.46, -27.98) * mm, "end": v(-42.46, -8.24) * mm});
            skCircle(sketch, "E98", {"center": v(-31.32, -8.24) * mm, "radius": 2 * mm});
            skLineSegment(sketch, "E99.bottom", {"start": v(42.46, 27.98) * mm, "end": v(16.14, 27.98) * mm});
            skLineSegment(sketch, "E99.left", {"start": v(42.46, 27.98) * mm, "end": v(42.46, 8.53) * mm});
            skCircle(sketch, "E100", {"center": v(18.13, 10.52) * mm, "radius": 2 * mm});
            skSolve(sketch);
        }
        {
            var Q0;
            Q0 = qSketchRegion(id + "F54", true);
            extrude(context, id + "F55", {"entities" : qUnion([Q0]), "operationType" : NewBodyOperationType.ADD, "depth" : 3.69 * mm, "offsetDistance" : 25 * mm, "hasDraft" : true, "draftAngle" : 10 * degree, "draftPullDirection" : true});
        }
        {
            var Q0;
            Q0=makeQuery(id+"F1.opExtrude","SWEPT_EDGE",EDGE,{"disambiguationData":[OSD([sQuery(id+"F0.wireOp",EDGE,"E0.top"),sQuery(id+"F0.wireOp",EDGE,"E0.right")])]});
            var Q1;
            Q1=makeQuery(id+"F1.opExtrude","SWEPT_EDGE",EDGE,{"disambiguationData":[OSD([sQuery(id+"F0.wireOp",EDGE,"E0.top"),sQuery(id+"F0.wireOp",EDGE,"E0.left")])]});
            var Q2;
            Q2=makeQuery(id+"F1.opExtrude","SWEPT_EDGE",EDGE,{"disambiguationData":[OSD([sQuery(id+"F0.wireOp",EDGE,"E0.bottom"),sQuery(id+"F0.wireOp",EDGE,"E0.left")])]});
            var Q3;
            Q3=makeQuery(id+"F1.opExtrude","SWEPT_EDGE",EDGE,{"disambiguationData":[OSD([sQuery(id+"F0.wireOp",EDGE,"E0.bottom"),sQuery(id+"F0.wireOp",EDGE,"E0.right")])]});
            fillet(context, id + "F56", {"entities" : qUnion([Q0, Q1, Q2, Q3]), "radius" : 3 * mm, "tangentPropagation" : true, "allowEdgeOverflow" : false});
        }
    });
